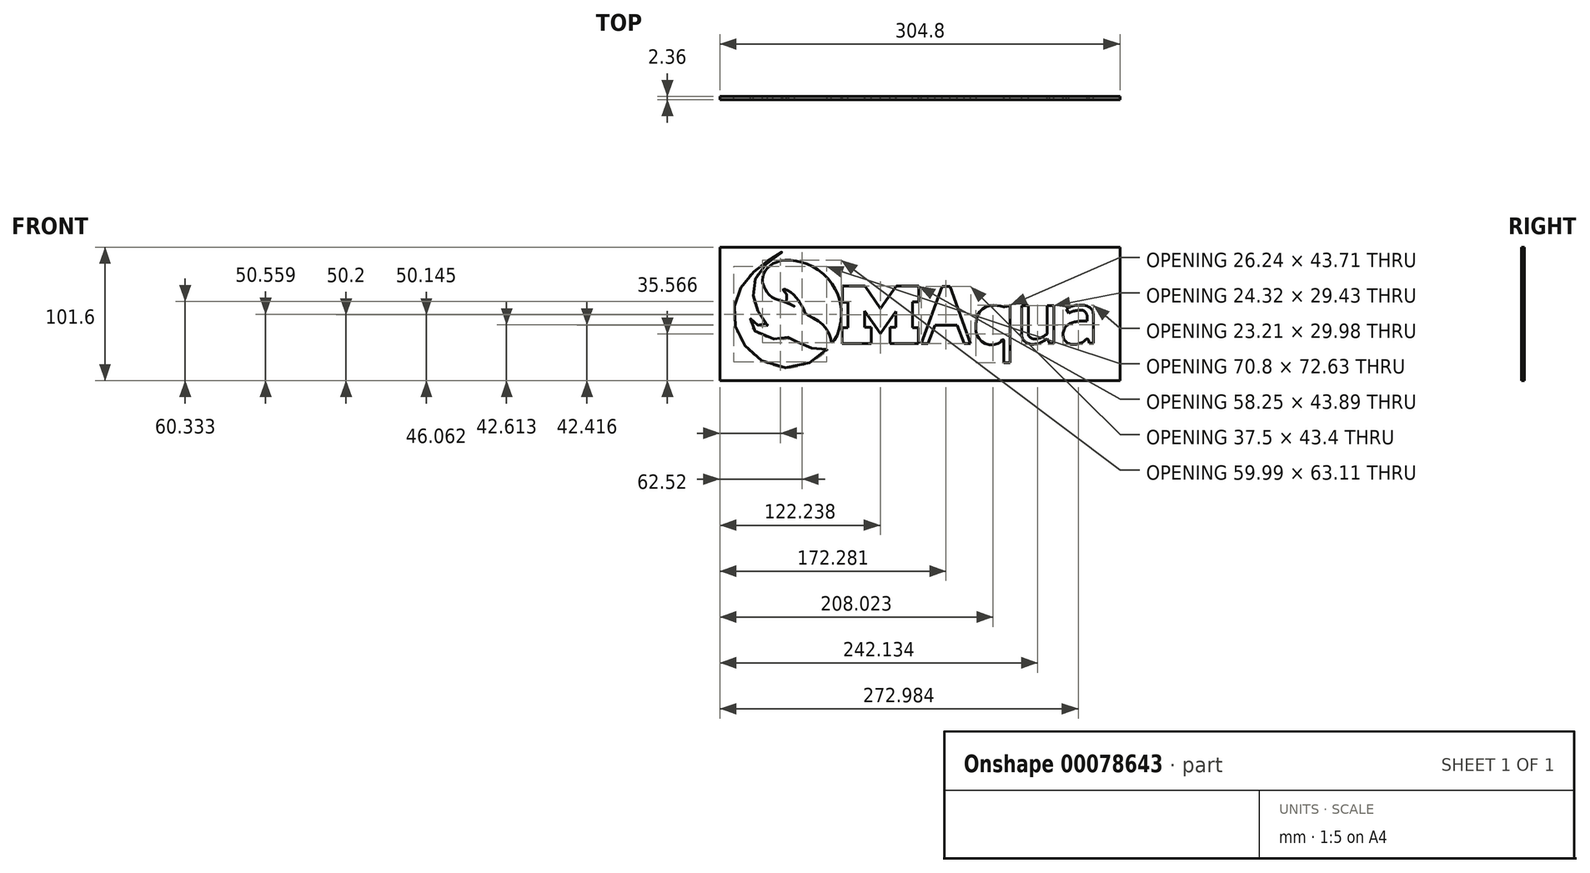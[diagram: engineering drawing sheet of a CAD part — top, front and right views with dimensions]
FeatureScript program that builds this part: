
annotation { "Feature Type Name" : "Feature", "Feature Type Description" : "" }
export const myFeature = defineFeature(function(context is Context, id is Id, definition is map)
    precondition{}
    {
        {
            var Q0;
            Q0=qCreatedBy(makeId("Front.planeOp"),FACE);
            var sketch = newSketch(context, id + "F0", { "sketchPlane" : qUnion([Q0])});
            skPoint(sketch, "E0", {"position": v(-51.5, 9.78) * mm});
            skFitSpline(sketch, "E1", {"points": [v(-63.52, 46.91) * mm, v(-58.95, 48.66) * mm, v(-53.16, 49.73) * mm, v(-43.94, 48.66) * mm, v(-35.41, 45.85) * mm, v(-25.44, 39.37) * mm, v(-17.37, 29.85) * mm, v(-13.7, 22.31) * mm, v(-11.7, 13.98) * mm, v(-11.6, 4.24) * mm, v(-15.5, -9.53) * mm, v(-19.08, -13.48) * mm], "startDerivative": vector(66.26, 27.47) * mm, "endDerivative": vector(-52.6, -41.7) * mm});
            skFitSpline(sketch, "E2", {"points": [v(-19.08, -13.48) * mm, v(-20.14, -8.2) * mm, v(-23.34, -2.21) * mm, v(-29.97, 3.79) * mm, v(-38.75, 9.03) * mm, v(-39.53, 10.95) * mm, v(-42.99, 17.08) * mm, v(-45.06, 20.3) * mm, v(-48.34, 23.86) * mm, v(-52.55, 26.57) * mm, v(-55.85, 27.56) * mm, v(-54.61, 25.37) * mm, v(-53.05, 23.03) * mm, v(-53.43, 17.94) * mm, v(-53.43, 17.94) * mm], "startDerivative": vector(-8.9, 67.38) * mm, "endDerivative": vector(-26.9, -14.26) * mm});
            skFitSpline(sketch, "E3", {"points": [v(-53.43, 17.94) * mm, v(-47.01, 14.27) * mm, v(-53.43, 17.17) * mm, v(-65.24, 22.18) * mm, v(-69.9, 28.84) * mm, v(-71.34, 32.51) * mm, v(-69.8, 40.52) * mm, v(-63.52, 46.91) * mm], "startDerivative": vector(70.3, -37.96) * mm, "endDerivative": vector(47.77, 36.4) * mm});
            skFitSpline(sketch, "E4", {"points": [v(-22.43, -18.55) * mm, v(-29.48, -18.55) * mm, v(-35.1, -17.11) * mm, v(-41.47, -14.62) * mm, v(-49.46, -10.3) * mm, v(-52.9, -8.19) * mm, v(-51.5, -10) * mm, v(-51.5, -10.56) * mm, v(-64.45, -10.25) * mm, v(-75.94, -5.6) * mm, v(-79.64, -1.19) * mm, v(-80.5, 4.4) * mm, v(-80.5, 5.26) * mm, v(-79.32, 3.06) * mm, v(-75.55, 0.15) * mm, v(-69.17, -0.87) * mm, v(-67.76, 0.07) * mm, v(-69.02, 1.8) * mm, v(-72.16, 5.9) * mm, v(-76.41, 14.23) * mm, v(-78.26, 20.44) * mm, v(-78.17, 29.23) * mm, v(-76.73, 35.92) * mm, v(-71.34, 43.55) * mm, v(-63.86, 50.94) * mm, v(-56.75, 55.7) * mm, v(-63.95, 51.87) * mm, v(-73.58, 43.64) * mm, v(-77.98, 40.65) * mm, v(-85.47, 32.41) * mm, v(-91.17, 20.72) * mm, v(-93.14, 12.3) * mm, v(-92.4, -0.2) * mm, v(-87.15, -12.44) * mm, v(-78.66, -22.06) * mm, v(-65.3, -30.18) * mm, v(-47.32, -32.17) * mm, v(-30.96, -25.93) * mm, v(-22.43, -18.55) * mm]});
            skLineSegment(sketch, "E5", {"start": v(49.64, -13.81) * mm, "end": v(65.5, 29.58) * mm});
            skLineSegment(sketch, "E6", {"start": v(65.5, 29.58) * mm, "end": v(71.53, 29.58) * mm});
            skLineSegment(sketch, "E7", {"start": v(71.53, 29.58) * mm, "end": v(87.14, -13.81) * mm});
            skLineSegment(sketch, "E8", {"start": v(87.14, -13.81) * mm, "end": v(82.1, -13.81) * mm});
            skLineSegment(sketch, "E9", {"start": v(82.1, -13.81) * mm, "end": v(76.81, 0) * mm});
            skLineSegment(sketch, "E10", {"start": v(76.81, 0) * mm, "end": v(59.85, 0) * mm});
            skLineSegment(sketch, "E11", {"start": v(59.85, 0) * mm, "end": v(54.68, -13.81) * mm});
            skLineSegment(sketch, "E12", {"start": v(54.68, -13.81) * mm, "end": v(49.64, -13.81) * mm});
            skLineSegment(sketch, "E13", {"start": v(68.08, 24.17) * mm, "end": v(61.7, 5) * mm});
            skLineSegment(sketch, "E14", {"start": v(61.7, 5) * mm, "end": v(74.84, 5) * mm});
            skLineSegment(sketch, "E15", {"start": v(68.08, 24.17) * mm, "end": v(74.84, 5) * mm});
            skFitSpline(sketch, "E16", {"points": [v(112.33, 13.89) * mm, v(117.04, 14.93) * mm], "startDerivative": vector(4.5, 1.55) * mm, "endDerivative": vector(4.5, 1.55) * mm});
            skFitSpline(sketch, "E17", {"points": [v(112.33, 13.89) * mm, v(107.32, 14.93) * mm, v(101.75, 14.93) * mm, v(95.32, 11.56) * mm, v(91.91, 5.9) * mm, v(90.98, -1.6) * mm, v(91.91, -7.41) * mm, v(96.71, -13.3) * mm, v(104, -14.85) * mm, v(110.27, -12.45) * mm, v(111.27, -10.97) * mm, v(112.33, -11.07) * mm, v(112.33, -12.07) * mm], "startDerivative": vector(-56.99, 21.47) * mm, "endDerivative": vector(-9.51, -62.49) * mm});
            skLineSegment(sketch, "E18", {"start": v(112.33, -12.07) * mm, "end": v(112.33, -28.55) * mm});
            skLineSegment(sketch, "E19", {"start": v(112.33, -28.55) * mm, "end": v(117.25, -28.55) * mm});
            skLineSegment(sketch, "E20", {"start": v(117.25, -28.55) * mm, "end": v(117.04, 14.93) * mm});
            skLineSegment(sketch, "E21", {"start": v(126.09, 14.83) * mm, "end": v(126.09, -7.83) * mm});
            skFitSpline(sketch, "E22", {"points": [v(126.09, -7.83) * mm, v(126.79, -10.56) * mm, v(130.92, -13.92) * mm, v(137.1, -14.26) * mm, v(142.8, -12.04) * mm, v(145.4, -10.22) * mm], "startDerivative": vector(1.56, -17.18) * mm, "endDerivative": vector(13.8, 10.85) * mm});
            skLineSegment(sketch, "E23", {"start": v(145.4, -10.22) * mm, "end": v(147.27, -13.9) * mm});
            skLineSegment(sketch, "E24", {"start": v(147.27, -13.9) * mm, "end": v(150.4, -13.9) * mm});
            skLineSegment(sketch, "E25", {"start": v(150.4, -13.9) * mm, "end": v(150.4, 14.87) * mm});
            skLineSegment(sketch, "E26", {"start": v(150.4, 14.87) * mm, "end": v(145.55, 14.87) * mm});
            skLineSegment(sketch, "E27", {"start": v(145.55, 14.87) * mm, "end": v(145.55, -6.63) * mm});
            skFitSpline(sketch, "E28", {"points": [v(145.55, -6.63) * mm, v(142.1, -8.76) * mm, v(137.92, -10.32) * mm, v(133.65, -10.07) * mm, v(131.1, -7.78) * mm], "startDerivative": vector(-13.36, -8.88) * mm, "endDerivative": vector(-9.64, 11.86) * mm});
            skLineSegment(sketch, "E29", {"start": v(131.1, -7.78) * mm, "end": v(131.1, 14.87) * mm});
            skLineSegment(sketch, "E30", {"start": v(131.1, 14.87) * mm, "end": v(126.09, 14.83) * mm});
            skFitSpline(sketch, "E31", {"points": [v(161.84, 9.06) * mm, v(165.67, 10.76) * mm, v(170.13, 11.38) * mm, v(173.06, 11.09) * mm, v(174.92, 9.23) * mm, v(175.83, 7.34) * mm], "startDerivative": vector(16, 8.61) * mm, "endDerivative": vector(4.73, -11.51) * mm});
            skLineSegment(sketch, "E32", {"start": v(175.83, 7.34) * mm, "end": v(175.83, 3.3) * mm});
            skFitSpline(sketch, "E33", {"points": [v(175.83, 3.3) * mm, v(170.1, 3.05) * mm, v(165.9, 2.33) * mm, v(161.8, 0.67) * mm, v(158.48, -2.72) * mm, v(157.5, -6.96) * mm], "startDerivative": vector(-26.98, -0.66) * mm, "endDerivative": vector(-2.44, -22.87) * mm});
            skFitSpline(sketch, "E34", {"points": [v(157.72, -6.96) * mm, v(157.5, -6.96) * mm, v(158.22, -10.7) * mm, v(161.6, -13.81) * mm, v(165.93, -14.7) * mm, v(170.49, -13.7) * mm, v(173.1, -12.42) * mm, v(175.62, -10.27) * mm, v(176.32, -10.45) * mm, v(177.56, -13.64) * mm], "startDerivative": vector(-8.2, 3.3) * mm, "endDerivative": vector(9.89, -32.64) * mm});
            skLineSegment(sketch, "E35", {"start": v(177.56, -13.64) * mm, "end": v(180.7, -13.64) * mm});
            skLineSegment(sketch, "E36", {"start": v(180.7, -13.64) * mm, "end": v(180.7, 8.33) * mm});
            skFitSpline(sketch, "E37", {"points": [v(180.7, 8.33) * mm, v(179.99, 11.1) * mm, v(178.62, 12.8) * mm, v(176.37, 14.32) * mm, v(173.7, 15.1) * mm, v(171.1, 15.37) * mm, v(168.33, 15.27) * mm, v(164.94, 14.55) * mm, v(161.82, 13.45) * mm, v(159.9, 12.27) * mm], "startDerivative": vector(-4.54, 26.43) * mm, "endDerivative": vector(-17.7, -12.17) * mm});
            skLineSegment(sketch, "E38", {"start": v(159.9, 12.27) * mm, "end": v(161.84, 9.06) * mm});
            skFitSpline(sketch, "E39", {"points": [v(175.64, -6.85) * mm, v(172.69, -8.74) * mm, v(168.96, -10.03) * mm, v(165.46, -10.17) * mm, v(163.66, -8.97) * mm, v(162.83, -6.94) * mm, v(163.53, -4.32) * mm, v(166.24, -1.97) * mm, v(169.51, -1) * mm, v(173.98, -0.73) * mm, v(175.54, -0.73) * mm], "startDerivative": vector(-26.13, -18.7) * mm, "endDerivative": vector(16.45, -2.69) * mm});
            skLineSegment(sketch, "E40", {"start": v(175.54, -0.73) * mm, "end": v(175.64, -6.85) * mm});
            skFitSpline(sketch, "E41", {"points": [v(112.03, 10.12) * mm, v(108.56, 11.14) * mm, v(104.66, 11.3) * mm, v(100.6, 9.63) * mm, v(97.63, 5.97) * mm, v(96.32, 0.46) * mm, v(96.6, -3.93) * mm, v(98.7, -8.18) * mm, v(101.73, -9.93) * mm, v(106.17, -10.18) * mm, v(110.42, -7.98) * mm, v(111.98, -7.1) * mm], "startDerivative": vector(-39.86, 13.71) * mm, "endDerivative": vector(20.6, 15.6) * mm});
            skLineSegment(sketch, "E42", {"start": v(112.03, 10.12) * mm, "end": v(111.98, -7.1) * mm});
            skLineSegment(sketch, "E43", {"start": v(-10.78, -13.9) * mm, "end": v(-10.78, -1.83) * mm});
            skLineSegment(sketch, "E44", {"start": v(-10.78, -1.83) * mm, "end": v(-6.3, -1.83) * mm});
            skLineSegment(sketch, "E45", {"start": v(-6.3, -1.83) * mm, "end": v(-6.3, 17.54) * mm});
            skLineSegment(sketch, "E46", {"start": v(-6.3, 17.54) * mm, "end": v(-10.54, 17.54) * mm});
            skLineSegment(sketch, "E47", {"start": v(-10.54, 17.54) * mm, "end": v(-10.54, 29.68) * mm});
            skLineSegment(sketch, "E48", {"start": v(-10.54, 29.68) * mm, "end": v(6.68, 29.68) * mm});
            skLineSegment(sketch, "E49", {"start": v(6.68, 29.68) * mm, "end": v(18.5, 12.57) * mm});
            skLineSegment(sketch, "E50", {"start": v(18.5, 12.57) * mm, "end": v(30.53, 29.88) * mm});
            skLineSegment(sketch, "E51", {"start": v(30.53, 29.88) * mm, "end": v(47.47, 29.88) * mm});
            skLineSegment(sketch, "E52", {"start": v(47.47, 29.88) * mm, "end": v(47.47, 17.63) * mm});
            skLineSegment(sketch, "E53", {"start": v(47.47, 17.63) * mm, "end": v(43, 17.63) * mm});
            skLineSegment(sketch, "E54", {"start": v(43, 17.63) * mm, "end": v(43, -1.76) * mm});
            skLineSegment(sketch, "E55", {"start": v(43, -1.76) * mm, "end": v(47.45, -1.76) * mm});
            skLineSegment(sketch, "E56", {"start": v(47.45, -1.76) * mm, "end": v(47.45, -13.95) * mm});
            skLineSegment(sketch, "E57", {"start": v(47.45, -13.95) * mm, "end": v(25.7, -13.95) * mm});
            skLineSegment(sketch, "E58", {"start": v(25.7, -13.95) * mm, "end": v(25.7, -1.72) * mm});
            skLineSegment(sketch, "E59", {"start": v(25.7, -1.72) * mm, "end": v(30.3, -1.72) * mm});
            skLineSegment(sketch, "E60", {"start": v(30.3, -1.72) * mm, "end": v(30.3, 10.4) * mm});
            skLineSegment(sketch, "E61", {"start": v(30.3, 10.4) * mm, "end": v(18.55, -6.33) * mm});
            skLineSegment(sketch, "E62", {"start": v(18.55, -6.33) * mm, "end": v(6.37, 10.78) * mm});
            skLineSegment(sketch, "E63", {"start": v(6.37, 10.78) * mm, "end": v(6.37, -1.7) * mm});
            skLineSegment(sketch, "E64", {"start": v(6.37, -1.7) * mm, "end": v(11.48, -1.7) * mm});
            skLineSegment(sketch, "E65", {"start": v(11.48, -1.7) * mm, "end": v(11.48, -14) * mm});
            skLineSegment(sketch, "E66", {"start": v(11.48, -14) * mm, "end": v(-10.78, -13.9) * mm});
            skLineSegment(sketch, "E67.bottom", {"start": v(-103.89, 59.34) * mm, "end": v(200.91, 59.34) * mm});
            skLineSegment(sketch, "E67.top", {"start": v(-103.89, -42.26) * mm, "end": v(200.91, -42.26) * mm});
            skLineSegment(sketch, "E67.left", {"start": v(-103.89, 59.34) * mm, "end": v(-103.89, -42.26) * mm});
            skLineSegment(sketch, "E67.right", {"start": v(200.91, 59.34) * mm, "end": v(200.91, -42.26) * mm});
            skSolve(sketch);
        }
        {
            var Q0;
            Q0 = qSketchRegion(id + "F0", true);
            extrude(context, id + "F1", {"entities" : qUnion([Q0]), "depth" : 2.36 * mm});
        }
    });
